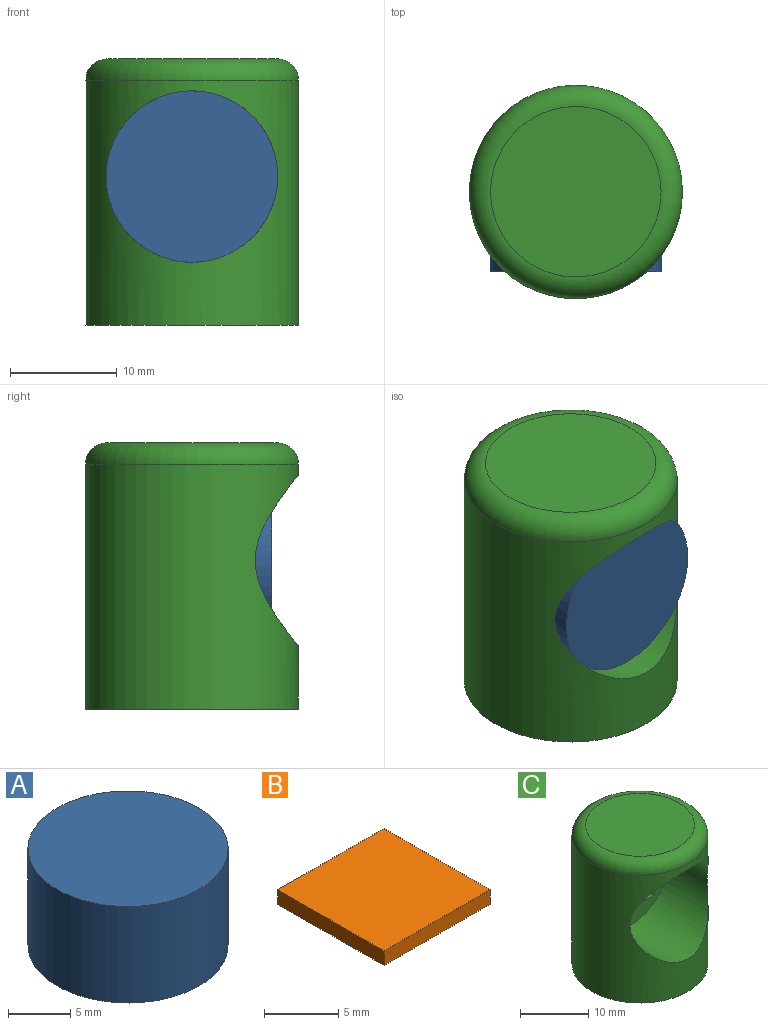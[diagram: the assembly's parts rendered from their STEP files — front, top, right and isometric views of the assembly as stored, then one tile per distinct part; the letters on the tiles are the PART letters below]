
ASSEMBLY  parts=3 mates=2
PART A: 3 faces, bbox 16.1x16.1x9.5 mm
  f0: cylinder r=8.05mm len=16.1mm, axis (0,0,-1), area 480.5mm2, adj f1,f2
  f1: plane 16.1x16.1mm, normal (0,0,1), area 203.6mm2, adj f0
  f2: plane 16.1x16.1mm, normal (0,0,-1), area 203.6mm2, adj f0
PART B: 6 faces, bbox 10.1x10.1x1.2 mm
  f0: plane 10.1x1.2mm, normal (0,-1,0), area 12.1mm2, adj f1,f3,f4,f5
  f1: plane 10.1x1.2mm, normal (1,0,0), area 12.1mm2, adj f0,f2,f4,f5
  f2: plane 10.1x1.2mm, normal (0,1,0), area 12.1mm2, adj f1,f3,f4,f5
  f3: plane 10.1x1.2mm, normal (-1,0,0), area 12.1mm2, adj f0,f2,f4,f5
  f4: plane 10.1x10.1mm, normal (0,0,1), area 102mm2, adj f0,f1,f2,f3
  f5: plane 10.1x10.1mm, normal (0,0,-1), area 102mm2, adj f0,f1,f2,f3
PART C: 11 faces, bbox 21.6x21.6x25 mm
  f0: plane 16.1x16.1mm, normal (0,-1,0), area 101.6mm2, adj f4,f5,f6,f7,f8
  f1: cylinder r=10mm len=23mm, axis (0,0,-1), area 1218.8mm2, adj f3,f4,f10
  f2: plane 16x16mm, normal (0,0,1), area 201.1mm2, adj f10
  f3: plane 20x20mm, normal (0,0,-1), area 314.2mm2, adj f1
  f4: cylinder r=8.05mm len=16.1mm, axis (0,-1,0), area 510.7mm2, adj f0,f1
  f5: plane 10.1x1.2mm, normal (0,0,1), area 12.1mm2, adj f0,f6,f8,f9
  f6: plane 10.1x1.2mm, normal (-1,0,0), area 12.1mm2, adj f0,f5,f7,f9
  f7: plane 10.1x1.2mm, normal (0,0,-1), area 12.1mm2, adj f0,f6,f8,f9
  f8: plane 10.1x1.2mm, normal (1,0,0), area 12.1mm2, adj f0,f5,f7,f9
  f9: plane 10.1x10.1mm, normal (0,-1,0), area 102mm2, adj f5,f6,f7,f8
  f10: torus R=8mm, axis (0,0,1), area 183mm2, adj f1,f2
PLACE A rot(axis=(1,0,0),90deg) t=(-26.83,28.99,3.24)mm
PLACE B rot(axis=(1,0,0),90deg) t=(-45.05,30.19,3.25)mm
PLACE C t=(-73.86,26.99,8.9)mm
MATE fastened B.f4 <-> A.f0  axis (0,-1,0) through (-73.86,28.99,22.85)mm
MATE fastened C.f4 <-> B.f5  axis (0,-1,0) through (-73.86,30.19,22.85)mm
